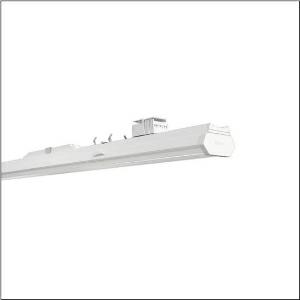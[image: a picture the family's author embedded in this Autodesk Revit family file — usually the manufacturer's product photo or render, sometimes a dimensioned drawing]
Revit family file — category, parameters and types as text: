
# Revit family: licross_r__11_protected_ho_51ts12dn5dxl_8709
name_source: partatom
category: Lighting Fixtures
units: mm (PartAtom-declared; Revit-internal decimal feet)

## family parameters
Cut with Voids When Loaded = No
Host = Face
Light Source = No
Part Type = Normal
Room Calculation Point = No
Round Connector Dimension = Use Diameter
Shared = No

## types (1)
- --- (1 x LED, 13380 lm, 86.1 W, 5000K)
    Apparent Load = 86 VA
    CIE Flux Codes = 54 82 95 97 100
    Color Rendering = 80
    Color Temperature = 5000K
    Default Elevation = 1800 mm
    Description = Licross® 11 Protected HOluminaire insert, length: 1.500mm, width: 90mm, height: 101mm, LED rated luminous flux: 13.380lm, light colour: 850, control gear: DALI 2, control gear: ECG DALI, with plug, 5-pole, with phase selection, mains connection: 220..240V, AC, 50/60Hz, halogen-free wiring, primary optical cover: cover, of PMMA, light emission: direct with ceiling illumination distribution, protection rating (complete): IP50, insulation class (complete): insulation class I (protective earthing), certification: CE, ENEC, VDE, protection symbol: D if used in an environment with non-conductive dust loads with corresponding accessories, permissible ambient temperature for indoor applications: -25..+35°C, reducing of maximum allowable ambient temperature of 5°C with ceiling mounting, corresponds to IFS (International Featured Standards) requirements for safety and quality in the food industry, packaging unit: 1 piece
    Height = 92 mm
    Lamp = 1 x LED
    Lamp Light Flux = 13380 lm
    Lamp Power = 86.1 W
    Lamp count = 1
    Length = 1500 mm
    Luminous efficacy = 155 lm/W
    Manufacturer = Siteco
    ModVariant = No
    Model = 51TS12DN5DXL
    Mounting Place = Ceiling
    Mounting Type = Pendant
    Number of Poles = 1
    OnlyDefault = Yes
    Power Factor = 1
    Product Name = Licross® 11 Protected HO
    Product group = luminaire insert
    ProductGroupID = 902
    Protection Class = Protection class I
    Protection Degree = IP 50
    RLX_Detail_Level = 1
    RlxData = <blob elided: 23909 chars, md5=ec9b7786>
    Socket = socket
    Standby Power = 0 W
    System Light Flux = 13380 lm
    System Power = 86 W
    Type Comments = factory setting: luminous flux: 100 % | dim-lin: 254 | 485 mA
    Type Image = l_1256145.jpg
    URL = http://relux.com
    VarID = @adj_138245
    Voltage = 0 V
    Weight = 0.00 kg
    Width = 88 mm

## geometry (parser evidence)
native form markers: Blend x4, Sweep x9
no freeform markers — native parametric forms only
